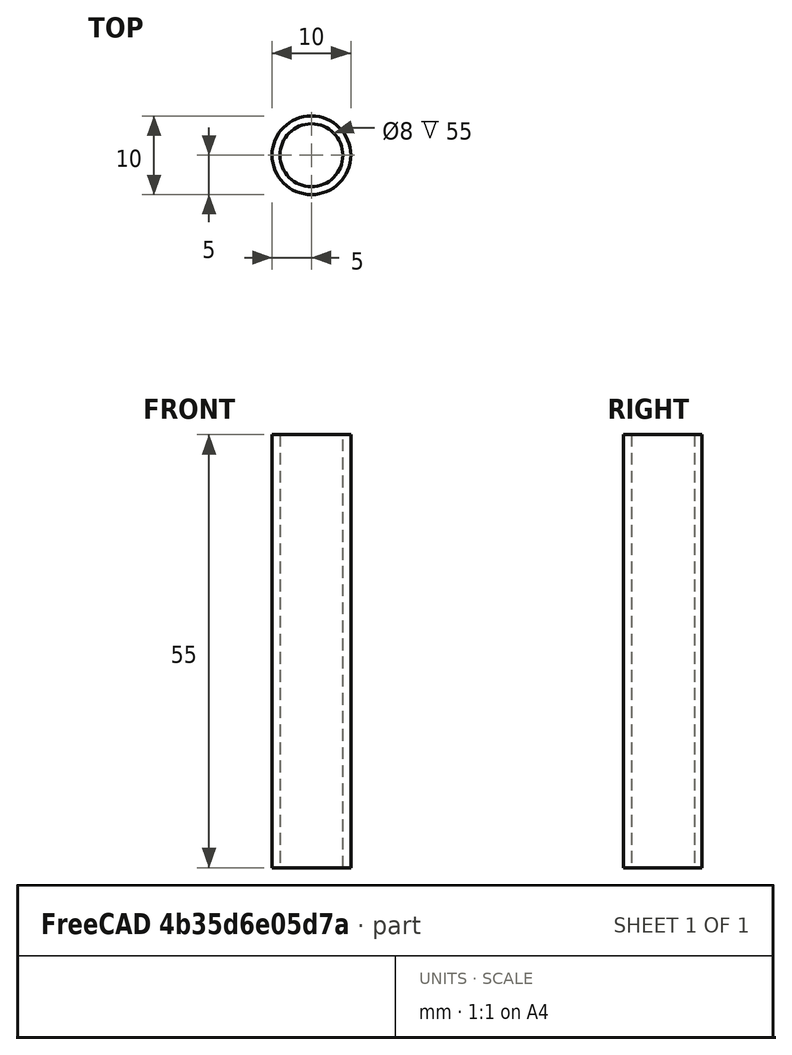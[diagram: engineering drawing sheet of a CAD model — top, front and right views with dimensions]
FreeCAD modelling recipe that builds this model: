
FCSTD DOCUMENT  (FreeCAD 0.19R24276 (Git))
Label: Tube_55_for_arm_80_W.CStd
License: All rights reserved
LicenseURL: http://en.wikipedia.org/wiki/All_rights_reserved
objects: Sketcher::SketchObject×1, PartDesign::Pad×1, PartDesign::Body×1
note: 4 computed .brp shape members not serialized (recipe doc carries the construction recipe); baked Part::Feature solids carry a one-line shape summary decoded from their .brp

FEATURE [Sketcher::SketchObject] Sketch
  FullyConstrained = true
  MapMode = 5
  Support = -> [XY_Plane]
  sketch-geometry (2):
    g0: Circle CenterX=0 CenterY=0 CenterZ=0 NormalX=0 NormalY=0 NormalZ=1 AngleXU=0 Radius=4
    g1: Circle CenterX=0 CenterY=0 CenterZ=0 NormalX=0 NormalY=0 NormalZ=1 AngleXU=0 Radius=5
  constraints (4):
    c: Coincident(g0,g-1)
    c: Coincident(g1,g0)
    c: Diameter(g0) = 8
    c: Diameter(g1) = 10
FEATURE [PartDesign::Pad] Pad
  Direction = (1,1,1)
  Length = 55
  Length2 = 100
  Profile = -> Sketch
  Type = 0
FEATURE [PartDesign::Body] Body
  Group = -> [Sketch,Pad]
  Origin = -> Origin
  Tip = -> Pad
